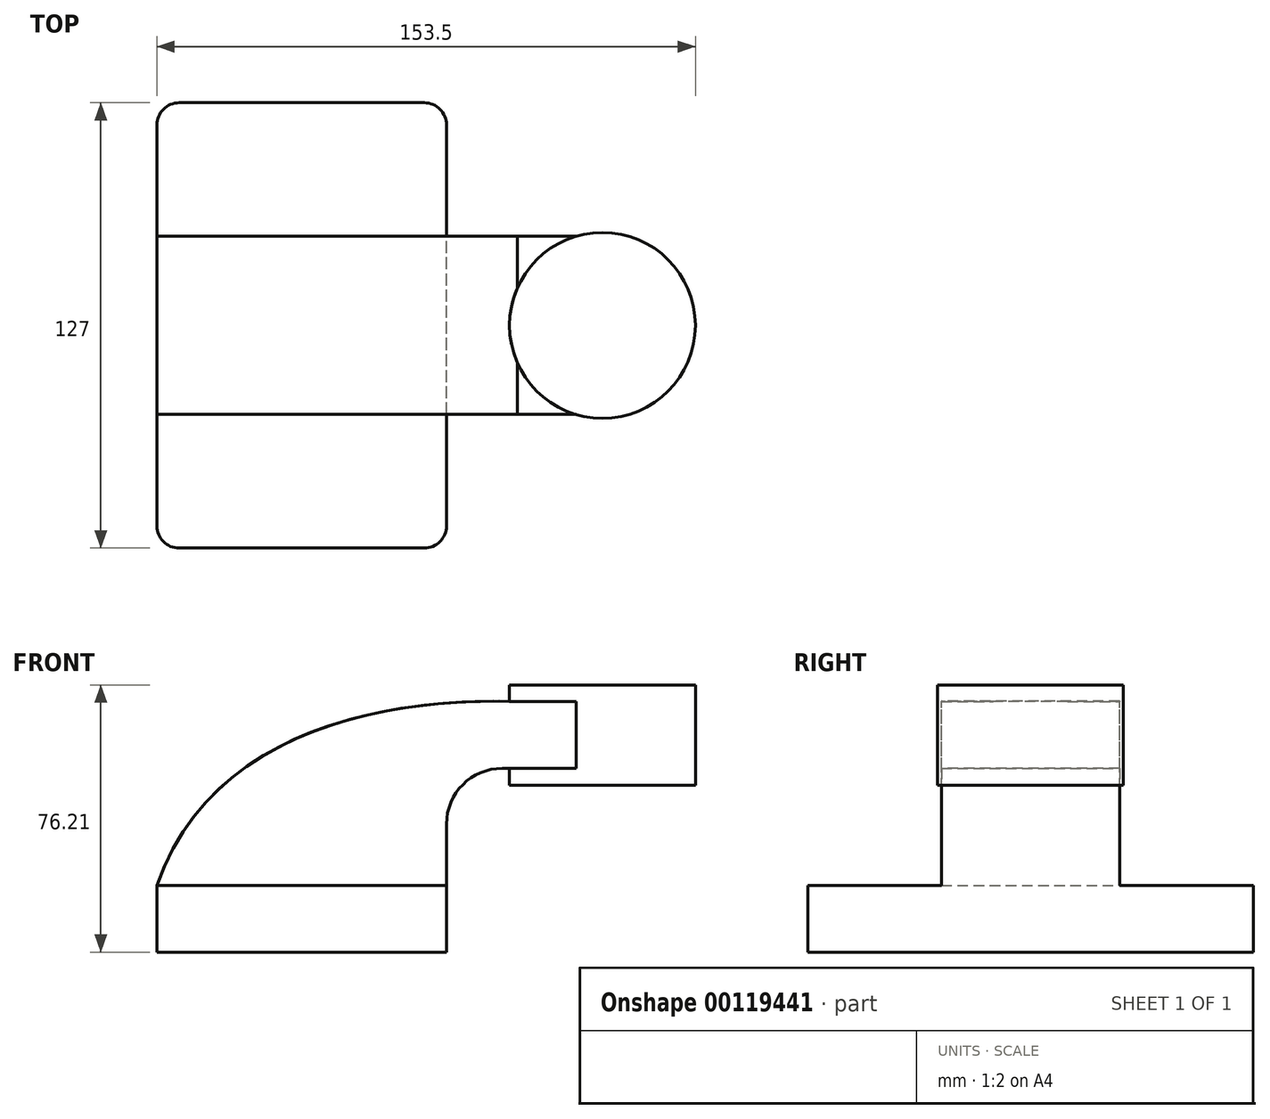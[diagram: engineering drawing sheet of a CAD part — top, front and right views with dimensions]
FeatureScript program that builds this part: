
annotation { "Feature Type Name" : "Feature", "Feature Type Description" : "" }
export const myFeature = defineFeature(function(context is Context, id is Id, definition is map)
    precondition{}
    {
        {
            var Q0;
            Q0=qCreatedBy(makeId("Front.planeOp"),FACE);
            var sketch = newSketch(context, id + "F0", { "sketchPlane" : qUnion([Q0])});
            skLineSegment(sketch, "E0.bottom", {"start": v(-41.28, -9.53) * mm, "end": v(41.28, -9.53) * mm});
            skLineSegment(sketch, "E0.top", {"start": v(-41.28, 9.53) * mm, "end": v(41.27, 9.53) * mm});
            skLineSegment(sketch, "E0.left", {"start": v(-41.27, -9.53) * mm, "end": v(-41.28, 9.53) * mm});
            skLineSegment(sketch, "E0.right", {"start": v(41.28, -9.53) * mm, "end": v(41.27, 9.53) * mm});
            skPoint(sketch, "E0.middle", {"position": v(0, 0) * mm});
            skLineSegment(sketch, "E1", {"start": v(41.27, 9.53) * mm, "end": v(41.27, 27) * mm});
            skLineSegment(sketch, "E2.bottom", {"start": v(61.42, 66.68) * mm, "end": v(112.22, 66.68) * mm});
            skLineSegment(sketch, "E2.top", {"start": v(61.42, 38.1) * mm, "end": v(112.22, 38.1) * mm});
            skLineSegment(sketch, "E2.left", {"start": v(61.42, 66.68) * mm, "end": v(61.42, 38.1) * mm});
            skLineSegment(sketch, "E2.right", {"start": v(112.22, 66.68) * mm, "end": v(112.22, 38.1) * mm});
            skArc(sketch, "E3", {"start": v(41.27, 27) * mm, "mid": v(45.92, 38.23) * mm, "end": v(57.15, 42.88) * mm});
            skLineSegment(sketch, "E4", {"start": v(57.15, 42.88) * mm, "end": v(85.72, 42.88) * mm});
            skLineSegment(sketch, "E5.0", {"start": v(57.15, 61.93) * mm, "end": v(85.72, 61.93) * mm});
            skArc(sketch, "E5.1", {"start": v(22.22, 27) * mm, "mid": v(32.45, 51.7) * mm, "end": v(57.15, 61.93) * mm});
            skLineSegment(sketch, "E5.2", {"start": v(22.22, 9.53) * mm, "end": v(22.22, 27) * mm});
            skPoint(sketch, "E6.1.internal.snap0", {"position": v(71.44, 61.93) * mm});
            skFitSpline(sketch, "E6", {"points": [v(-41.28, 9.52) * mm, v(61.42, 61.93) * mm], "startDerivative": vector(45.09, 130.35) * mm, "endDerivative": vector(117.94, -3.63) * mm});
            skLineSegment(sketch, "E7", {"start": v(85.72, 42.88) * mm, "end": v(85.72, 66.68) * mm});
            skLineSegment(sketch, "E8", {"start": v(85.72, 66.68) * mm, "end": v(85.72, 42.88) * mm});
            skLineSegment(sketch, "E9", {"start": v(85.72, 61.93) * mm, "end": v(85.72, 38.1) * mm});
            skPoint(sketch, "E9.endSnap0", {"position": v(86.82, 38.1) * mm});
            skSolve(sketch);
        }
        {
            var Q0;
            Q0=makeQuery(id+"F0.imprint","IMPRINT",FACE,{"disambiguationData":[TD([[makeQuery(id+"F0.imprint","IMPRINT",EDGE,{"derivedFrom":sQuery(id+"F0.wireOp",EDGE,"E0.bottom")}),1.0]])]});
            extrude(context, id + "F1", {"entities" : qUnion([Q0]), "endBound" : BoundingType.SYMMETRIC, "depth" : 127 * mm});
        }
        {
            var Q0;
            {var subQ1=sQuery(id+"F0.wireOp",EDGE,"E1");Q0=makeQuery(id+"F0.imprint","IMPRINT",FACE,{"disambiguationData":[TD([[makeQuery(id+"F0.imprint","IMPRINT",EDGE,{"derivedFrom":subQ1}),1.0]])]});}
            var Q1;
            {var subQ0=sQuery(id+"F0.wireOp",EDGE,"E5.1");var subQ1=sQuery(id+"F0.wireOp",EDGE,"E5.0");var subQ2=makeQuery(id+"F0.imprint","INTERSECT",VERTEX,{"derivedFrom":[subQ1,subQ0]});Q1=makeQuery(id+"F0.imprint","IMPRINT",FACE,{"disambiguationData":[TD([[makeQuery(id+"F0.imprint","IMPRINT",EDGE,{"disambiguationData":[TD([[subQ2,1.0]])],"derivedFrom":subQ0}),-1.0]])]});}
            extrude(context, id + "F2", {"entities" : qUnion([Q0, Q1]), "operationType" : NewBodyOperationType.ADD, "endBound" : BoundingType.SYMMETRIC, "depth" : 50.8 * mm});
        }
        {
            var Q0;
            {var subQ3=sQuery(id+"F0.wireOp",EDGE,"E4");var subQ5=sQuery(id+"F0.wireOp",EDGE,"E9");var subQ6=makeQuery(id+"F0.imprint","INTERSECT",VERTEX,{"derivedFrom":[subQ3,subQ5]});Q0=makeQuery(id+"F0.imprint","IMPRINT",FACE,{"disambiguationData":[TD([[makeQuery(id+"F0.imprint","IMPRINT",EDGE,{"disambiguationData":[TD([[subQ6,1.0]])],"derivedFrom":subQ3}),1.0]])]});}
            extrude(context, id + "F3", {"entities" : qUnion([Q0]), "operationType" : NewBodyOperationType.ADD, "endBound" : BoundingType.SYMMETRIC, "depth" : 50.8 * mm});
        }
        {
            var Q0;
            {var subQ0=sQuery(id+"F0.wireOp",EDGE,"E2.right");Q0=makeQuery(id+"F0.imprint","IMPRINT",FACE,{"disambiguationData":[TD([[makeQuery(id+"F0.imprint","IMPRINT",EDGE,{"derivedFrom":subQ0}),-1.0]])]});}
            var Q1;
            Q1=sQuery(id+"F0.wireOp",EDGE,"E8");
            revolve(context, id + "F4", {"operationType" : NewBodyOperationType.ADD, "entities" : qUnion([Q0]), "axis" : qUnion([Q1]), "revolveType" : RevolveType.FULL});
        }
        {
            var Q0;
            {var subQ3=sQuery(id+"F0.wireOp",EDGE,"E5.2");Q0=makeQuery(id+"F0.imprint","IMPRINT",FACE,{"disambiguationData":[TD([[makeQuery(id+"F0.imprint","IMPRINT",EDGE,{"derivedFrom":subQ3}),1.0]])]});}
            extrude(context, id + "F5", {"entities" : qUnion([Q0]), "operationType" : NewBodyOperationType.ADD, "endBound" : BoundingType.SYMMETRIC, "depth" : 15.88 * mm});
        }
        {
            var Q0;
            Q0=makeQuery(id+"F1.opExtrude","CAP_EDGE",EDGE,{"disambiguationData":[OSD([sQuery(id+"F0.wireOp",EDGE,"E0.right")])],"isStart":true});
            var Q1;
            Q1=makeQuery(id+"F1.opExtrude","CAP_EDGE",EDGE,{"disambiguationData":[OSD([sQuery(id+"F0.wireOp",EDGE,"E0.left")])],"isStart":true});
            var Q2;
            Q2=makeQuery(id+"F1.opExtrude","CAP_EDGE",EDGE,{"disambiguationData":[OSD([sQuery(id+"F0.wireOp",EDGE,"E0.left")])],"isStart":false});
            var Q3;
            Q3=makeQuery(id+"F1.opExtrude","CAP_EDGE",EDGE,{"disambiguationData":[OSD([sQuery(id+"F0.wireOp",EDGE,"E0.right")])],"isStart":false});
            fillet(context, id + "F6", {"entities" : qUnion([Q0, Q1, Q2, Q3]), "radius" : 6.35 * mm, "tangentPropagation" : true, "allowEdgeOverflow" : false});
        }
    });
